annotation { "Feature Type Name" : "Feature", "Feature Type Description" : "" }
export const myFeature = defineFeature(function(context is Context, id is Id, definition is map)
    precondition{}
    {
        {
            var Q0;
            Q0=qCreatedBy(makeId("Top.planeOp"),FACE);
            var sketch = newSketch(context, id + "F0", { "sketchPlane" : qUnion([Q0])});
            skLineSegment(sketch, "E0.bottom", {"start": v(76.2, -76.2) * mm, "end": v(-76.2, -76.2) * mm});
            skLineSegment(sketch, "E0.top", {"start": v(76.2, 76.2) * mm, "end": v(-76.2, 76.2) * mm});
            skLineSegment(sketch, "E0.left", {"start": v(76.2, -76.2) * mm, "end": v(76.2, 76.2) * mm});
            skLineSegment(sketch, "E0.right", {"start": v(-76.2, -76.2) * mm, "end": v(-76.2, 76.2) * mm});
            skPoint(sketch, "E0.middle", {"position": v(0, 0) * mm});
            skSolve(sketch);
        }
        {
            var Q0;
            Q0 = qSketchRegion(id + "F0", true);
            extrude(context, id + "F1", {"entities" : qUnion([Q0]), "depth" : 152.4 * mm});
        }
        {
            var Q0;
            Q0=makeQuery(id+"F1.opExtrude","CAP_FACE",FACE,{"disambiguationData":[OSD([sQuery(id+"F0.wireOp",EDGE,"E0.bottom"),sQuery(id+"F0.wireOp",EDGE,"E0.top"),sQuery(id+"F0.wireOp",EDGE,"E0.left"),sQuery(id+"F0.wireOp",EDGE,"E0.right")])],"isStart":false});
            var sketch = newSketch(context, id + "F2", { "sketchPlane" : qUnion([Q0])});
            skLineSegment(sketch, "E1.bottom", {"start": v(50.06, 30.55) * mm, "end": v(-1.58, 30.55) * mm});
            skLineSegment(sketch, "E1.top", {"start": v(50.06, 53.8) * mm, "end": v(-1.58, 53.8) * mm});
            skLineSegment(sketch, "E1.left", {"start": v(50.06, 30.55) * mm, "end": v(50.06, 53.8) * mm});
            skLineSegment(sketch, "E1.right", {"start": v(-1.58, 30.55) * mm, "end": v(-1.58, 53.8) * mm});
            skPoint(sketch, "E1.middle", {"position": v(24.24, 42.17) * mm});
            skLineSegment(sketch, "E2.bottom", {"start": v(44.34, -69.37) * mm, "end": v(13.6, -69.37) * mm});
            skLineSegment(sketch, "E2.top", {"start": v(44.34, -9.07) * mm, "end": v(13.6, -9.07) * mm});
            skLineSegment(sketch, "E2.left", {"start": v(44.34, -69.37) * mm, "end": v(44.34, -9.07) * mm});
            skLineSegment(sketch, "E2.right", {"start": v(13.6, -69.37) * mm, "end": v(13.6, -9.07) * mm});
            skPoint(sketch, "E2.middle", {"position": v(28.97, -39.22) * mm});
            skLineSegment(sketch, "E3.bottom", {"start": v(-25.82, -40.4) * mm, "end": v(-53.4, -40.4) * mm});
            skLineSegment(sketch, "E3.top", {"start": v(-25.82, -27.79) * mm, "end": v(-53.4, -27.79) * mm});
            skLineSegment(sketch, "E3.left", {"start": v(-25.82, -40.4) * mm, "end": v(-25.82, -27.79) * mm});
            skLineSegment(sketch, "E3.right", {"start": v(-53.4, -40.4) * mm, "end": v(-53.4, -27.79) * mm});
            skPoint(sketch, "E3.middle", {"position": v(-39.61, -34.1) * mm});
            skSolve(sketch);
        }
        {
            var Q0;
            Q0 = qSketchRegion(id + "F2", true);
            extrude(context, id + "F3", {"entities" : qUnion([Q0]), "operationType" : NewBodyOperationType.ADD, "depth" : 0 * mm});
        }
        {
            var Q0;
            Q0=makeQuery(id+"F3.opExtrude","CAP_FACE",FACE,{"disambiguationData":[OSD([sQuery(id+"F2.wireOp",EDGE,"E1.bottom"),sQuery(id+"F2.wireOp",EDGE,"E1.top"),sQuery(id+"F2.wireOp",EDGE,"E1.left"),sQuery(id+"F2.wireOp",EDGE,"E1.right")])],"isStart":false});
            var Q1;
            Q1=makeQuery(id+"F3.opExtrude","CAP_FACE",FACE,{"disambiguationData":[OSD([sQuery(id+"F2.wireOp",EDGE,"E2.bottom"),sQuery(id+"F2.wireOp",EDGE,"E2.top"),sQuery(id+"F2.wireOp",EDGE,"E2.left"),sQuery(id+"F2.wireOp",EDGE,"E2.right")])],"isStart":false});
            var Q2;
            Q2=makeQuery(id+"F3.opExtrude","CAP_FACE",FACE,{"disambiguationData":[OSD([sQuery(id+"F2.wireOp",EDGE,"E3.bottom"),sQuery(id+"F2.wireOp",EDGE,"E3.top"),sQuery(id+"F2.wireOp",EDGE,"E3.left"),sQuery(id+"F2.wireOp",EDGE,"E3.right")])],"isStart":false});
            shell(context, id + "F4", {"entities" : qUnion([Q0, Q1, Q2]), "thickness" : 2.54 * mm});
        }
        {
            var Q0;
            Q0=makeQuery(id+"F1.opExtrude","SWEPT_FACE",FACE,{"disambiguationData":[OSD([sQuery(id+"F0.wireOp",EDGE,"E0.right")])]});
            var sketch = newSketch(context, id + "F5", { "sketchPlane" : qUnion([Q0])});
            skLineSegment(sketch, "E4.bottom", {"start": v(76.2, 0) * mm, "end": v(8.57, 0) * mm});
            skLineSegment(sketch, "E4.top", {"start": v(76.2, 152.4) * mm, "end": v(8.57, 152.4) * mm});
            skLineSegment(sketch, "E4.left", {"start": v(76.2, 0) * mm, "end": v(76.2, 152.4) * mm});
            skLineSegment(sketch, "E4.right", {"start": v(8.57, 0) * mm, "end": v(8.57, 152.4) * mm});
            skSolve(sketch);
        }
        {
            var Q0;
            Q0 = qSketchRegion(id + "F5", true);
            extrude(context, id + "F6", {"entities" : qUnion([Q0]), "operationType" : NewBodyOperationType.ADD, "depth" : 76.2 * mm});
        }
        {
            var Q0;
            Q0=makeQuery(id+"F6.boolean.opBoolean","MERGE",FACE,{"derivedFrom":[makeQuery(id+"F1.opExtrude","CAP_FACE",FACE,{"disambiguationData":[OSD([sQuery(id+"F0.wireOp",EDGE,"E0.bottom"),sQuery(id+"F0.wireOp",EDGE,"E0.top"),sQuery(id+"F0.wireOp",EDGE,"E0.left"),sQuery(id+"F0.wireOp",EDGE,"E0.right")])],"isStart":false}),makeQuery(id+"F6.opExtrude","SWEPT_FACE",FACE,{"disambiguationData":[OSD([sQuery(id+"F5.wireOp",EDGE,"E4.top")])]})]});
            var sketch = newSketch(context, id + "F7", { "sketchPlane" : qUnion([Q0])});
            skLineSegment(sketch, "E5.bottom", {"start": v(-142.7, -76.2) * mm, "end": v(-81.01, -76.2) * mm});
            skLineSegment(sketch, "E5.top", {"start": v(-142.7, -22.57) * mm, "end": v(-81.01, -22.57) * mm});
            skLineSegment(sketch, "E5.left", {"start": v(-142.7, -76.2) * mm, "end": v(-142.7, -22.57) * mm});
            skLineSegment(sketch, "E5.right", {"start": v(-81.01, -76.2) * mm, "end": v(-81.01, -22.57) * mm});
            skSolve(sketch);
        }
        {
            var Q0;
            Q0 = qSketchRegion(id + "F7", true);
            extrude(context, id + "F8", {"entities" : qUnion([Q0]), "operationType" : NewBodyOperationType.ADD, "depth" : 0 * mm});
        }
        {
            var Q0;
            Q0=makeQuery(id+"F8.opExtrude","CAP_FACE",FACE,{"disambiguationData":[OSD([sQuery(id+"F7.wireOp",EDGE,"E5.bottom"),sQuery(id+"F7.wireOp",EDGE,"E5.top"),sQuery(id+"F7.wireOp",EDGE,"E5.left"),sQuery(id+"F7.wireOp",EDGE,"E5.right")])],"isStart":false});
            shell(context, id + "F9", {"entities" : qUnion([Q0]), "thickness" : 2.54 * mm});
        }
        {
            var Q0;
            Q0=makeQuery(id+"F6.boolean.opBoolean","MERGE",FACE,{"derivedFrom":[makeQuery(id+"F1.opExtrude","CAP_FACE",FACE,{"disambiguationData":[OSD([sQuery(id+"F0.wireOp",EDGE,"E0.bottom"),sQuery(id+"F0.wireOp",EDGE,"E0.top"),sQuery(id+"F0.wireOp",EDGE,"E0.left"),sQuery(id+"F0.wireOp",EDGE,"E0.right")])],"isStart":false}),makeQuery(id+"F6.opExtrude","SWEPT_FACE",FACE,{"disambiguationData":[OSD([sQuery(id+"F5.wireOp",EDGE,"E4.top")])]})]});
            var sketch = newSketch(context, id + "F10", { "sketchPlane" : qUnion([Q0])});
            skText(sketch, "E6", { "text": "Barbie House", "fontName": "OpenSans-Regular.ttf"});
            const initialGuessF10  = {"E6": [-0.02022, 0.06302, 1, 0, 0.00603]};
            skSetInitialGuess(sketch, initialGuessF10);
            skSolve(sketch);
        }
        {
            var Q0;
            Q0 = qSketchRegion(id + "F10", true);
            extrude(context, id + "F11", {"entities" : qUnion([Q0]), "operationType" : NewBodyOperationType.ADD, "depth" : 0 * mm});
        }
        {
            var Q0;
            {var subQ0=sQuery(id+"F0.wireOp",EDGE,"E0.bottom");var subQ2=sQuery(id+"F0.wireOp",EDGE,"E0.top");var subQ4=sQuery(id+"F5.wireOp",EDGE,"E4.top");var subQ5=sQuery(id+"F0.wireOp",EDGE,"E0.left");var subQ6=sQuery(id+"F0.wireOp",EDGE,"E0.right");Q0=makeQuery(id+"F11.boolean.opBoolean","SPLIT",FACE,{"disambiguationData":[TD([makeQuery(id+"F1.opExtrude","SWEPT_FACE",FACE,{"disambiguationData":[OSD([subQ0])]})])],"derivedFrom":makeQuery(id+"F6.boolean.opBoolean","MERGE",FACE,{"derivedFrom":[makeQuery(id+"F1.opExtrude","CAP_FACE",FACE,{"disambiguationData":[OSD([subQ0,subQ2,subQ5,subQ6])],"isStart":false}),makeQuery(id+"F6.opExtrude","SWEPT_FACE",FACE,{"disambiguationData":[OSD([subQ4])]})]})});}
            var sketch = newSketch(context, id + "F12", { "sketchPlane" : qUnion([Q0])});
            skCircle(sketch, "E7", {"center": v(-61, 14.96) * mm, "radius": 4.1 * mm});
            skPoint(sketch, "E7.first.point", {"position": v(-59.04, 18.56) * mm});
            skPoint(sketch, "E7.second.point", {"position": v(-63.35, 11.62) * mm});
            skPoint(sketch, "E7.third.point", {"position": v(-61.8, 10.95) * mm});
            skCircle(sketch, "E8", {"center": v(-42.8, 7.15) * mm, "radius": 3.3 * mm});
            skCircle(sketch, "E9", {"center": v(-30.32, 1) * mm, "radius": 4.57 * mm});
            skPoint(sketch, "E9.first.point", {"position": v(-29.14, 5.41) * mm});
            skPoint(sketch, "E9.second.point", {"position": v(-32.29, -3.13) * mm});
            skPoint(sketch, "E9.third.point", {"position": v(-30.28, -3.58) * mm});
            skCircle(sketch, "E10", {"center": v(-13.85, -0.23) * mm, "radius": 2.01 * mm});
            skPoint(sketch, "E10.first.point", {"position": v(-14.01, 1.78) * mm});
            skPoint(sketch, "E10.second.point", {"position": v(-13.96, -2.23) * mm});
            skPoint(sketch, "E10.third.point", {"position": v(-13.74, -2.23) * mm});
            skCircle(sketch, "E11", {"center": v(-3.24, -3.77) * mm, "radius": 4.05 * mm});
            skPoint(sketch, "E11.first.point", {"position": v(-3.2, 0.27) * mm});
            skPoint(sketch, "E11.second.point", {"position": v(-3.2, -7.82) * mm});
            skPoint(sketch, "E11.second.point.positionSnap0", {"position": v(-3.2, 0.27) * mm});
            skPoint(sketch, "E11.third.point", {"position": v(-5.47, -7.15) * mm});
            skCircle(sketch, "E12", {"center": v(11.5, -2.6) * mm, "radius": 2.97 * mm});
            skPoint(sketch, "E12.first.point", {"position": v(9.54, -0.37) * mm});
            skPoint(sketch, "E12.second.point", {"position": v(10.4, -5.36) * mm});
            skPoint(sketch, "E12.third.point", {"position": v(9.95, -5.14) * mm});
            skCircle(sketch, "E13", {"center": v(25.07, -2.58) * mm, "radius": 3.03 * mm});
            skPoint(sketch, "E13.first.point", {"position": v(24.58, 0.41) * mm});
            skPoint(sketch, "E13.second.point", {"position": v(24.7, -5.59) * mm});
            skPoint(sketch, "E13.third.point", {"position": v(23.14, -4.92) * mm});
            skCircle(sketch, "E14", {"center": v(35.62, -1) * mm, "radius": 3.03 * mm});
            skPoint(sketch, "E14.first.point", {"position": v(35, 1.95) * mm});
            skPoint(sketch, "E14.second.point", {"position": v(35.88, -4.02) * mm});
            skPoint(sketch, "E14.third.point", {"position": v(37.22, -3.58) * mm});
            skCircle(sketch, "E15", {"center": v(47.1, -0.28) * mm, "radius": 5.25 * mm});
            skPoint(sketch, "E15.first.point", {"position": v(44, 3.96) * mm});
            skPoint(sketch, "E15.second.point", {"position": v(49.96, -4.7) * mm});
            skPoint(sketch, "E15.third.point", {"position": v(51.52, -3.13) * mm});
            skCircle(sketch, "E16", {"center": v(59, 5.84) * mm, "radius": 2.77 * mm});
            skPoint(sketch, "E16.first.point", {"position": v(57.96, 8.4) * mm});
            skPoint(sketch, "E16.second.point", {"position": v(59.57, 3.13) * mm});
            skPoint(sketch, "E16.third.point", {"position": v(57.78, 3.35) * mm});
            skCircle(sketch, "E17", {"center": v(67.96, 9.7) * mm, "radius": 2.82 * mm});
            skPoint(sketch, "E17.first.point", {"position": v(66.03, 11.76) * mm});
            skPoint(sketch, "E17.second.point", {"position": v(69.85, 7.6) * mm});
            skPoint(sketch, "E17.third.point", {"position": v(68.5, 6.93) * mm});
            skSolve(sketch);
        }
        {
            var Q0;
            Q0 = qSketchRegion(id + "F12", true);
            extrude(context, id + "F13", {"entities" : qUnion([Q0]), "operationType" : NewBodyOperationType.ADD, "depth" : 2.54 * mm});
        }
        {
            var Q0;
            {var subQ0=sQuery(id+"F0.wireOp",EDGE,"E0.bottom");var subQ2=sQuery(id+"F0.wireOp",EDGE,"E0.top");var subQ4=sQuery(id+"F5.wireOp",EDGE,"E4.top");var subQ5=sQuery(id+"F0.wireOp",EDGE,"E0.left");var subQ6=sQuery(id+"F0.wireOp",EDGE,"E0.right");Q0=makeQuery(id+"F11.boolean.opBoolean","SPLIT",FACE,{"disambiguationData":[TD([makeQuery(id+"F1.opExtrude","SWEPT_FACE",FACE,{"disambiguationData":[OSD([subQ0])]})])],"derivedFrom":makeQuery(id+"F6.boolean.opBoolean","MERGE",FACE,{"derivedFrom":[makeQuery(id+"F1.opExtrude","CAP_FACE",FACE,{"disambiguationData":[OSD([subQ0,subQ2,subQ5,subQ6])],"isStart":false}),makeQuery(id+"F6.opExtrude","SWEPT_FACE",FACE,{"disambiguationData":[OSD([subQ4])]})]})});}
            var sketch = newSketch(context, id + "F14", { "sketchPlane" : qUnion([Q0])});
            skArc(sketch, "E18", {"start": v(-74.53, 26.15) * mm, "mid": v(-2.25, 0.8) * mm, "end": v(72.98, 15.2) * mm});
            skArc(sketch, "E19", {"start": v(-74.53, 26.15) * mm, "mid": v(-2.24, 0.97) * mm, "end": v(72.98, 15.2) * mm});
            skSolve(sketch);
        }
        {
            var Q0;
            Q0 = qSketchRegion(id + "F14", true);
            extrude(context, id + "F15", {"entities" : qUnion([Q0]), "operationType" : NewBodyOperationType.ADD, "depth" : 0 * mm});
        }
    });